# Revit family: ASL_Designline_Al_Door_Head
name_source: partatom
category: Detail Items
revit_build: Autodesk Revit 2018 (Build: 20170223_1515(x64)
units: mm (PartAtom-declared; Revit-internal decimal feet)

## family parameters
Rotate with component = No
Section Shape = Not Defined
Shared = Yes

## types (3) — shared parameters
Head = Yes
Manufacturer = Aluminate Solutions Limited
Technical Info = www.aluminate.nz

## per-type parameters (varying)
| type | 50mm Door Jamb Standard | Glazing | Masking Region Parametric | Top&Bottom Rail 100mm | Top&Bottom Rail 75mm | Type Comments |
| Glazing | No | Yes | 22 mm | No | No | ASL Designline Head With Glazing |
| Single Action ASL Door Suite 100mm | Yes | No | 31 mm  [stored 0.101706 ft] | Yes | No | ASL Designline Head With Single Action ASL 100mm Door Suite |
| Single Action ASL Door Suite 75mm | Yes | No | 31 mm  [stored 0.101706 ft] | No | Yes | ASL Designline Head With Single Action ASL 75mm Door Suite |

note: [stored X ft] marks values corroborated as IEEE doubles in the binary element streams (Revit-internal decimal feet)

## geometry (parser evidence)
native form markers: Sweep x6
no freeform markers — native parametric forms only
